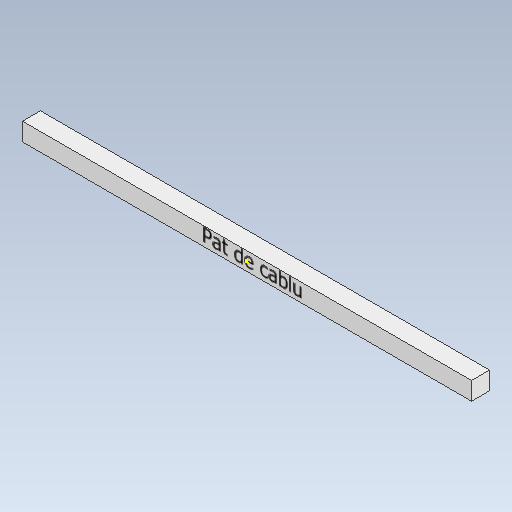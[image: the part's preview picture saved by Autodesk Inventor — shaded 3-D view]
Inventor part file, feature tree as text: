
AUTODESK INVENTOR PART (.ipt)
format: ipt  version: 2020 (Build 240168000, 168)  size: 97,280 bytes
history: native  units: mm
features: sketch x2, extrude x1
ambient origin geometry x8: Origin, YZ Plane, XZ Plane, XY Plane, X Axis, Y Axis, Z Axis, Center Point
bodies: Solid1 (feature_tree)
feature tree (3):
  extrude  "Extrusion1"  Depth=500.0mm
  sketch  "Sketch2"  dims[d2=20.0mm d3=0.0mm]
  sketch  "Sketch1"  dims[d0=20.0mm d1=500.0mm]
